# Revit family: Entablature
name_source: partatom
category: Lighting Fixtures
revit_build: Autodesk Revit 2013 (Build: 20130531_2115(x64)
units: mm (PartAtom-declared; Revit-internal decimal feet)

## types (2) — shared parameters
Apparent Load = 0 VA
Assembly Code = D5020200
Color Filter = 16777215
Description = Site/Roadway Luminare
Dimming Lamp Color Temperature Shift = <None>
Emit Shape Visible in Rendering = No
Emit from Rectangle Length = 0' - 10"
Emit from Rectangle Width = 0' - 10"
Finish = Powder Coat-Kim-Platinum Silver
Lens = Glass-KIM-Temper Molded
Load Classification = Lighting
Manufacturer = KIM Lighting
Manufacturer Fax = 626-369-2695
MasterFormat Title = Parking Lighting, Roadway Lighting, Site Lighting
Note Text = LF
Note Visible = Yes
Number of Poles = 1
Offset from Pole = 0' - 5"
Photometric Notes = More IES files download on Photometric Web Link
Photometric Web Link = http://www.kimlighting.com
Pole = Yes
Pole Height = 20' - 0"
Pole Width = 0' - 5"
Power Factor = 1
Product Documentation Link = http://www.kimlighting.com
Product Page URL = http://www.kimlighting.com
Revisions Date = 10/20/2017
Series = Entablature
Tilt Angle = 90.00°
Type Comments = Lighting Fixture
URL = http://www.kimlighting.com
Voltage = 0 V

## per-type parameters (varying)
| type | Arch Height | Depth | Fixture Height | Lamp | Model | Photometric Web File | Wattage Comments | Width |
| Large LED | 0' - 2" | 1' - 11" | 0' - 8" | 80 LEDs | ET | et2e35-96l4k.ies | 92W for 350mA, 188W for 700mA ET LED | 1' - 4" |
| Small LED | 0' - 1 1/2" | 1' - 5 1/2" | 0' - 6" | 40 LEDs, | SET | set3-070s-hs.ies | 45W for 350mA, 93W for 700mA SET LED | 1' - 0" |

## geometry (parser evidence)
native form markers: Sweep x4
no freeform markers — native parametric forms only
